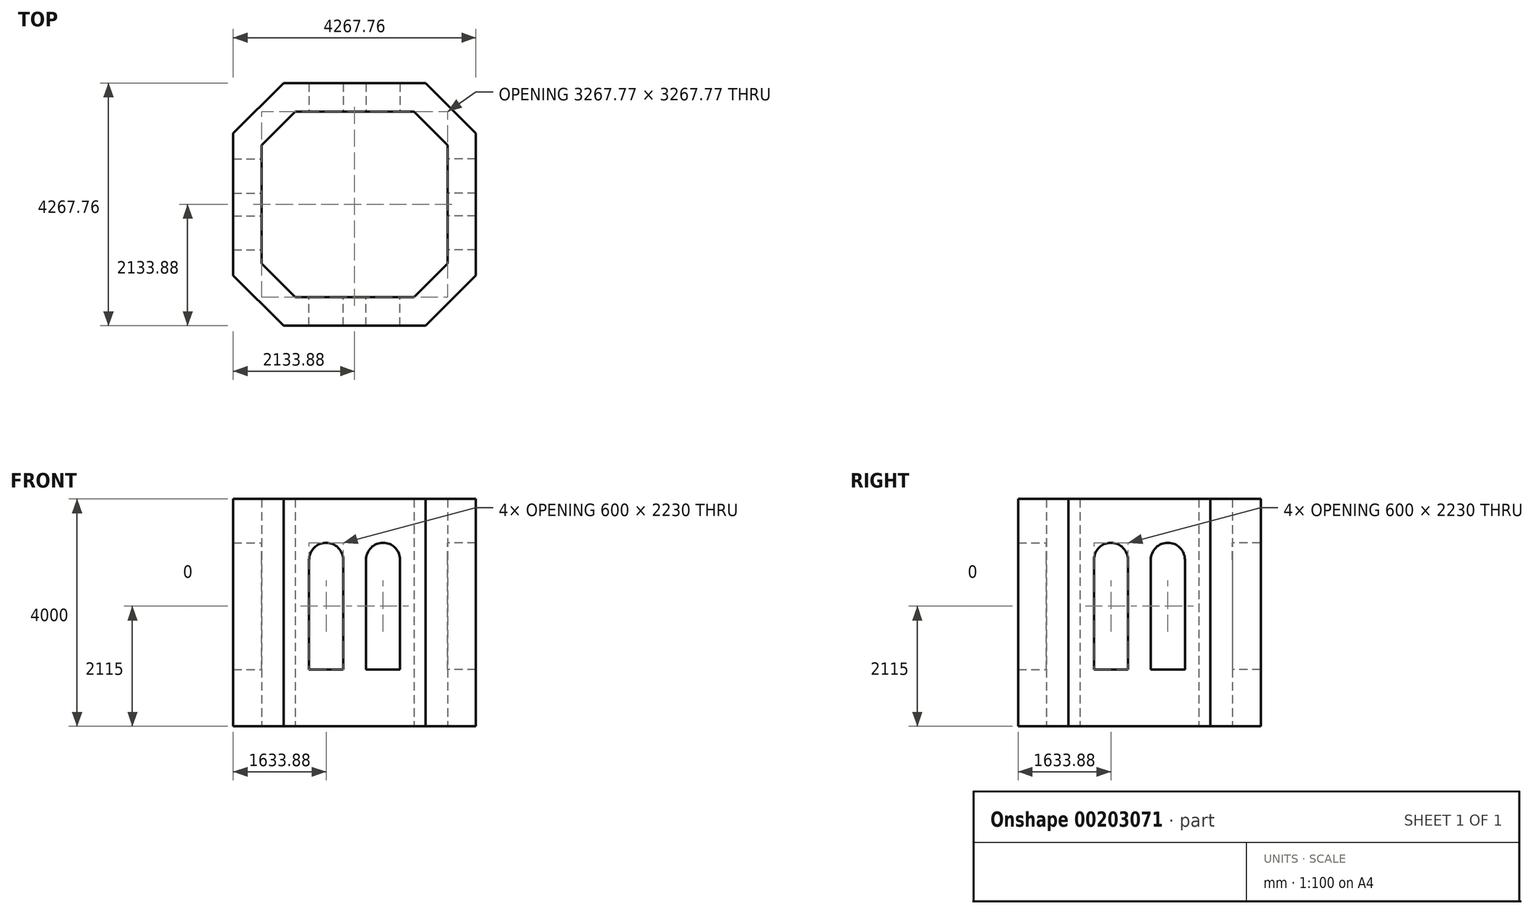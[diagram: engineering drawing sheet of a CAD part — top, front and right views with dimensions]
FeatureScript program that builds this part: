
annotation { "Feature Type Name" : "Feature", "Feature Type Description" : "" }
export const myFeature = defineFeature(function(context is Context, id is Id, definition is map)
    precondition{}
    {
        {
            var Q0;
            Q0=qCreatedBy(makeId("Top.planeOp"),FACE);
            var sketch = newSketch(context, id + "F0", { "sketchPlane" : qUnion([Q0])});
            skLineSegment(sketch, "E0", {"start": v(0, 2269.64) * mm, "end": v(0, -2162.41) * mm, "construction": true});
            skLineSegment(sketch, "E1", {"start": v(-2496.65, 0) * mm, "end": v(2670.15, 0) * mm, "construction": true});
            skLineSegment(sketch, "E2", {"start": v(-1250, 2133.88) * mm, "end": v(1250, 2133.88) * mm});
            skPoint(sketch, "E3", {"position": v(0, 2133.88) * mm});
            skLineSegment(sketch, "E4.MirrorCS", {"start": v(-1250, -2133.88) * mm, "end": v(1250, -2133.88) * mm});
            skLineSegment(sketch, "E5", {"start": v(1250, 2133.88) * mm, "end": v(2133.88, 1250) * mm});
            skLineSegment(sketch, "E6", {"start": v(-1250, 2133.88) * mm, "end": v(-2133.88, 1250) * mm});
            skLineSegment(sketch, "E7", {"start": v(-2133.88, 1250) * mm, "end": v(-2133.88, -1250) * mm});
            skLineSegment(sketch, "E8", {"start": v(-2133.88, -1250) * mm, "end": v(-1250, -2133.88) * mm});
            skLineSegment(sketch, "E9", {"start": v(1250, -2133.88) * mm, "end": v(2133.88, -1250) * mm});
            skLineSegment(sketch, "E10", {"start": v(2133.88, -1250) * mm, "end": v(2133.88, 1250) * mm});
            skPoint(sketch, "E11", {"position": v(-2133.88, 0) * mm});
            skPoint(sketch, "E12", {"position": v(2133.88, 0) * mm});
            skLineSegment(sketch, "E13.0", {"start": v(1042.9, -1633.88) * mm, "end": v(1633.88, -1042.9) * mm});
            skLineSegment(sketch, "E13.1", {"start": v(-1042.9, -1633.88) * mm, "end": v(1042.9, -1633.88) * mm});
            skLineSegment(sketch, "E13.2", {"start": v(1633.88, -1042.9) * mm, "end": v(1633.88, 1042.9) * mm});
            skLineSegment(sketch, "E13.3", {"start": v(-1633.88, -1042.9) * mm, "end": v(-1042.9, -1633.88) * mm});
            skLineSegment(sketch, "E13.4", {"start": v(1042.9, 1633.88) * mm, "end": v(1633.88, 1042.9) * mm});
            skLineSegment(sketch, "E13.5", {"start": v(-1042.9, 1633.88) * mm, "end": v(1042.9, 1633.88) * mm});
            skLineSegment(sketch, "E13.6", {"start": v(-1042.9, 1633.88) * mm, "end": v(-1633.88, 1042.9) * mm});
            skLineSegment(sketch, "E13.7", {"start": v(-1633.88, 1042.9) * mm, "end": v(-1633.88, -1042.9) * mm});
            skSolve(sketch);
        }
        {
            var Q0;
            Q0 = qSketchRegion(id + "F0", true);
            extrude(context, id + "F1", {"entities" : qUnion([Q0]), "depth" : 4000 * mm, "offsetDistance" : 25 * mm});
        }
        {
            var Q0;
            Q0=makeQuery(id+"F1.opExtrude","CAP_FACE",FACE,{"disambiguationData":[OSD([sQuery(id+"F0.wireOp",EDGE,"E2"),sQuery(id+"F0.wireOp",EDGE,"E4.MirrorCS"),sQuery(id+"F0.wireOp",EDGE,"E5"),sQuery(id+"F0.wireOp",EDGE,"E6"),sQuery(id+"F0.wireOp",EDGE,"E7"),sQuery(id+"F0.wireOp",EDGE,"E8"),sQuery(id+"F0.wireOp",EDGE,"E9"),sQuery(id+"F0.wireOp",EDGE,"E10")])],"isStart":true});
            cPlane(context, id + "F2", {"entities" : qUnion([Q0]), "cplaneType" : CPlaneType.OFFSET, "offset" : 1000 * mm, "oppositeDirection" : true, "width" : 150 * mm, "height" : 150 * mm});
        }
        {
            var Q0;
            Q0=qCreatedBy(id+"F2.planeOp",FACE);
            var sketch = newSketch(context, id + "F3", { "sketchPlane" : qUnion([Q0])});
            skLineSegment(sketch, "E14", {"start": v(-2830.43, 0) * mm, "end": v(2639.13, 0) * mm, "construction": true});
            skLineSegment(sketch, "E15", {"start": v(0, -2343.48) * mm, "end": v(0, 2126.09) * mm, "construction": true});
            skLineSegment(sketch, "E16.bottom", {"start": v(-800, -2500) * mm, "end": v(-200, -2500) * mm});
            skLineSegment(sketch, "E16.top", {"start": v(-800, -1250) * mm, "end": v(-200, -1250) * mm});
            skLineSegment(sketch, "E16.left", {"start": v(-800, -2500) * mm, "end": v(-800, -1250) * mm});
            skLineSegment(sketch, "E16.right", {"start": v(-200, -2500) * mm, "end": v(-200, -1250) * mm});
            skLineSegment(sketch, "E17.MirrorCS", {"start": v(200, -2500) * mm, "end": v(200, -1250) * mm});
            skLineSegment(sketch, "E18.MirrorCS", {"start": v(800, -2500) * mm, "end": v(200, -2500) * mm});
            skLineSegment(sketch, "E19.MirrorCS", {"start": v(800, -2500) * mm, "end": v(800, -1250) * mm});
            skLineSegment(sketch, "E20.MirrorCS", {"start": v(800, -1250) * mm, "end": v(200, -1250) * mm});
            skLineSegment(sketch, "E21.1.0", {"start": v(-2500, 800) * mm, "end": v(-2500, 200) * mm});
            skLineSegment(sketch, "E21.1.1", {"start": v(-2500, 800) * mm, "end": v(-1250, 800) * mm});
            skLineSegment(sketch, "E21.1.2", {"start": v(-2500, 200) * mm, "end": v(-1250, 200) * mm});
            skLineSegment(sketch, "E21.1.3", {"start": v(-1250, 800) * mm, "end": v(-1250, 200) * mm});
            skLineSegment(sketch, "E21.1.4", {"start": v(-2500, -200) * mm, "end": v(-1250, -200) * mm});
            skLineSegment(sketch, "E21.1.5", {"start": v(-2500, -800) * mm, "end": v(-1250, -800) * mm});
            skLineSegment(sketch, "E21.1.6", {"start": v(-2500, -800) * mm, "end": v(-2500, -200) * mm});
            skLineSegment(sketch, "E21.1.7", {"start": v(-1250, -800) * mm, "end": v(-1250, -200) * mm});
            skLineSegment(sketch, "E21.2.0", {"start": v(800, 2500) * mm, "end": v(200, 2500) * mm});
            skLineSegment(sketch, "E21.2.1", {"start": v(800, 2500) * mm, "end": v(800, 1250) * mm});
            skLineSegment(sketch, "E21.2.2", {"start": v(200, 2500) * mm, "end": v(200, 1250) * mm});
            skLineSegment(sketch, "E21.2.3", {"start": v(800, 1250) * mm, "end": v(200, 1250) * mm});
            skLineSegment(sketch, "E21.2.4", {"start": v(-200, 2500) * mm, "end": v(-200, 1250) * mm});
            skLineSegment(sketch, "E21.2.5", {"start": v(-800, 2500) * mm, "end": v(-800, 1250) * mm});
            skLineSegment(sketch, "E21.2.6", {"start": v(-800, 2500) * mm, "end": v(-200, 2500) * mm});
            skLineSegment(sketch, "E21.2.7", {"start": v(-800, 1250) * mm, "end": v(-200, 1250) * mm});
            skLineSegment(sketch, "E21.3.0", {"start": v(2500, -800) * mm, "end": v(2500, -200) * mm});
            skLineSegment(sketch, "E21.3.1", {"start": v(2500, -800) * mm, "end": v(1250, -800) * mm});
            skLineSegment(sketch, "E21.3.2", {"start": v(2500, -200) * mm, "end": v(1250, -200) * mm});
            skLineSegment(sketch, "E21.3.3", {"start": v(1250, -800) * mm, "end": v(1250, -200) * mm});
            skLineSegment(sketch, "E21.3.4", {"start": v(2500, 200) * mm, "end": v(1250, 200) * mm});
            skLineSegment(sketch, "E21.3.5", {"start": v(2500, 800) * mm, "end": v(1250, 800) * mm});
            skLineSegment(sketch, "E21.3.6", {"start": v(2500, 800) * mm, "end": v(2500, 200) * mm});
            skLineSegment(sketch, "E21.3.7", {"start": v(1250, 800) * mm, "end": v(1250, 200) * mm});
            skPoint(sketch, "E21.center", {"position": v(0, 0) * mm});
            skLineSegment(sketch, "E21.anchor1", {"start": v(0, 0) * mm, "end": v(-800, -2500) * mm, "construction": true});
            skLineSegment(sketch, "E21.anchor2", {"start": v(0, 0) * mm, "end": v(2500, -800) * mm, "construction": true});
            skSolve(sketch);
        }
        {
            var Q0;
            Q0 = qSketchRegion(id + "F3", true);
            extrude(context, id + "F4", {"entities" : qUnion([Q0]), "operationType" : NewBodyOperationType.REMOVE, "oppositeDirection" : true, "depth" : 2230 * mm, "offsetDistance" : 25 * mm});
        }
        {
            var Q0;
            Q0=makeQuery(id+"F4.boolean.opBoolean","COPY",EDGE,{"derivedFrom":makeQuery(id+"F4.opExtrude","CAP_EDGE",EDGE,{"disambiguationData":[OSD([sQuery(id+"F3.wireOp",EDGE,"E21.1.1")])],"isStart":false})});
            var Q1;
            Q1=makeQuery(id+"F4.boolean.opBoolean","COPY",EDGE,{"derivedFrom":makeQuery(id+"F4.opExtrude","CAP_EDGE",EDGE,{"disambiguationData":[OSD([sQuery(id+"F3.wireOp",EDGE,"E21.1.2")])],"isStart":false})});
            var Q2;
            Q2=makeQuery(id+"F4.boolean.opBoolean","COPY",EDGE,{"derivedFrom":makeQuery(id+"F4.opExtrude","CAP_EDGE",EDGE,{"disambiguationData":[OSD([sQuery(id+"F3.wireOp",EDGE,"E21.1.5")])],"isStart":false})});
            var Q3;
            Q3=makeQuery(id+"F4.boolean.opBoolean","COPY",EDGE,{"derivedFrom":makeQuery(id+"F4.opExtrude","CAP_EDGE",EDGE,{"disambiguationData":[OSD([sQuery(id+"F3.wireOp",EDGE,"E21.1.4")])],"isStart":false})});
            var Q4;
            Q4=makeQuery(id+"F4.boolean.opBoolean","COPY",EDGE,{"derivedFrom":makeQuery(id+"F4.opExtrude","CAP_EDGE",EDGE,{"disambiguationData":[OSD([sQuery(id+"F3.wireOp",EDGE,"E16.right")])],"isStart":false})});
            var Q5;
            Q5=makeQuery(id+"F4.boolean.opBoolean","COPY",EDGE,{"derivedFrom":makeQuery(id+"F4.opExtrude","CAP_EDGE",EDGE,{"disambiguationData":[OSD([sQuery(id+"F3.wireOp",EDGE,"E19.MirrorCS")])],"isStart":false})});
            var Q6;
            Q6=makeQuery(id+"F4.boolean.opBoolean","COPY",EDGE,{"derivedFrom":makeQuery(id+"F4.opExtrude","CAP_EDGE",EDGE,{"disambiguationData":[OSD([sQuery(id+"F3.wireOp",EDGE,"E16.left")])],"isStart":false})});
            var Q7;
            Q7=makeQuery(id+"F4.boolean.opBoolean","COPY",EDGE,{"derivedFrom":makeQuery(id+"F4.opExtrude","CAP_EDGE",EDGE,{"disambiguationData":[OSD([sQuery(id+"F3.wireOp",EDGE,"E17.MirrorCS")])],"isStart":false})});
            var Q8;
            Q8=makeQuery(id+"F4.boolean.opBoolean","COPY",EDGE,{"derivedFrom":makeQuery(id+"F4.opExtrude","CAP_EDGE",EDGE,{"disambiguationData":[OSD([sQuery(id+"F3.wireOp",EDGE,"E21.3.2")])],"isStart":false})});
            var Q9;
            Q9=makeQuery(id+"F4.boolean.opBoolean","COPY",EDGE,{"derivedFrom":makeQuery(id+"F4.opExtrude","CAP_EDGE",EDGE,{"disambiguationData":[OSD([sQuery(id+"F3.wireOp",EDGE,"E21.3.5")])],"isStart":false})});
            var Q10;
            Q10=makeQuery(id+"F4.boolean.opBoolean","COPY",EDGE,{"derivedFrom":makeQuery(id+"F4.opExtrude","CAP_EDGE",EDGE,{"disambiguationData":[OSD([sQuery(id+"F3.wireOp",EDGE,"E21.3.1")])],"isStart":false})});
            var Q11;
            Q11=makeQuery(id+"F4.boolean.opBoolean","COPY",EDGE,{"derivedFrom":makeQuery(id+"F4.opExtrude","CAP_EDGE",EDGE,{"disambiguationData":[OSD([sQuery(id+"F3.wireOp",EDGE,"E21.3.4")])],"isStart":false})});
            var Q12;
            Q12=makeQuery(id+"F4.boolean.opBoolean","COPY",EDGE,{"derivedFrom":makeQuery(id+"F4.opExtrude","CAP_EDGE",EDGE,{"disambiguationData":[OSD([sQuery(id+"F3.wireOp",EDGE,"E21.2.2")])],"isStart":false})});
            var Q13;
            Q13=makeQuery(id+"F4.boolean.opBoolean","COPY",EDGE,{"derivedFrom":makeQuery(id+"F4.opExtrude","CAP_EDGE",EDGE,{"disambiguationData":[OSD([sQuery(id+"F3.wireOp",EDGE,"E21.2.5")])],"isStart":false})});
            var Q14;
            Q14=makeQuery(id+"F4.boolean.opBoolean","COPY",EDGE,{"derivedFrom":makeQuery(id+"F4.opExtrude","CAP_EDGE",EDGE,{"disambiguationData":[OSD([sQuery(id+"F3.wireOp",EDGE,"E21.2.1")])],"isStart":false})});
            var Q15;
            Q15=makeQuery(id+"F4.boolean.opBoolean","COPY",EDGE,{"derivedFrom":makeQuery(id+"F4.opExtrude","CAP_EDGE",EDGE,{"disambiguationData":[OSD([sQuery(id+"F3.wireOp",EDGE,"E21.2.4")])],"isStart":false})});
            fillet(context, id + "F5", {"entities" : qUnion([Q0, Q1, Q2, Q3, Q4, Q5, Q6, Q7, Q8, Q9, Q10, Q11, Q12, Q13, Q14, Q15]), "radius" : 300 * mm, "tangentPropagation" : true, "allowEdgeOverflow" : false});
        }
    });
